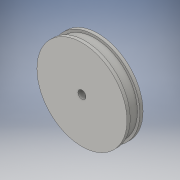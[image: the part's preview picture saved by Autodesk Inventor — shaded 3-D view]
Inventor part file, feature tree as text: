
AUTODESK INVENTOR PART (.ipt)
format: ipt  version: 2016 (Build 200138000, 138)  size: 120,320 bytes
history: native  units: mm
features: sketch x4, extrude x3, hole x1
ambient origin geometry x8: Origin, YZ Plane, XZ Plane, XY Plane, X Axis, Y Axis, Z Axis, Center Point
bodies: Solid1 (feature_tree)
feature tree (8):
  extrude  "Extrusion1"  Depth=1.0mm TaperAngle=0.0deg
  extrude  "Extrusion2"  Depth=3.0mm TaperAngle=0.0deg
  extrude  "Extrusion3"  Depth=1.0mm TaperAngle=0.0deg
  hole  "Hole1"  [1 undecoded]
  sketch  "Sketch1"  dims[d0=28.0mm d1=1.0mm d2=0.0mm]
  sketch  "Sketch2"  dims[d4=26.5mm d5=3.0mm d6=0.0mm]
  sketch  "Sketch3"  dims[d7=28.0mm d8=1.0mm d9=0.0mm]
  sketch  "Sketch4"  dims[d10=2.5mm d11=2.5mm d12=6.0mm d13=4.0mm d14=2.0mm d15=90.0deg d16=0.5mm d17=20.594885mm]
note: 1 required parameter value undecoded (feature->parameter linkage not recoverable at this tier; creation-order binding heuristic only, values carry confidence <= 0.55)
